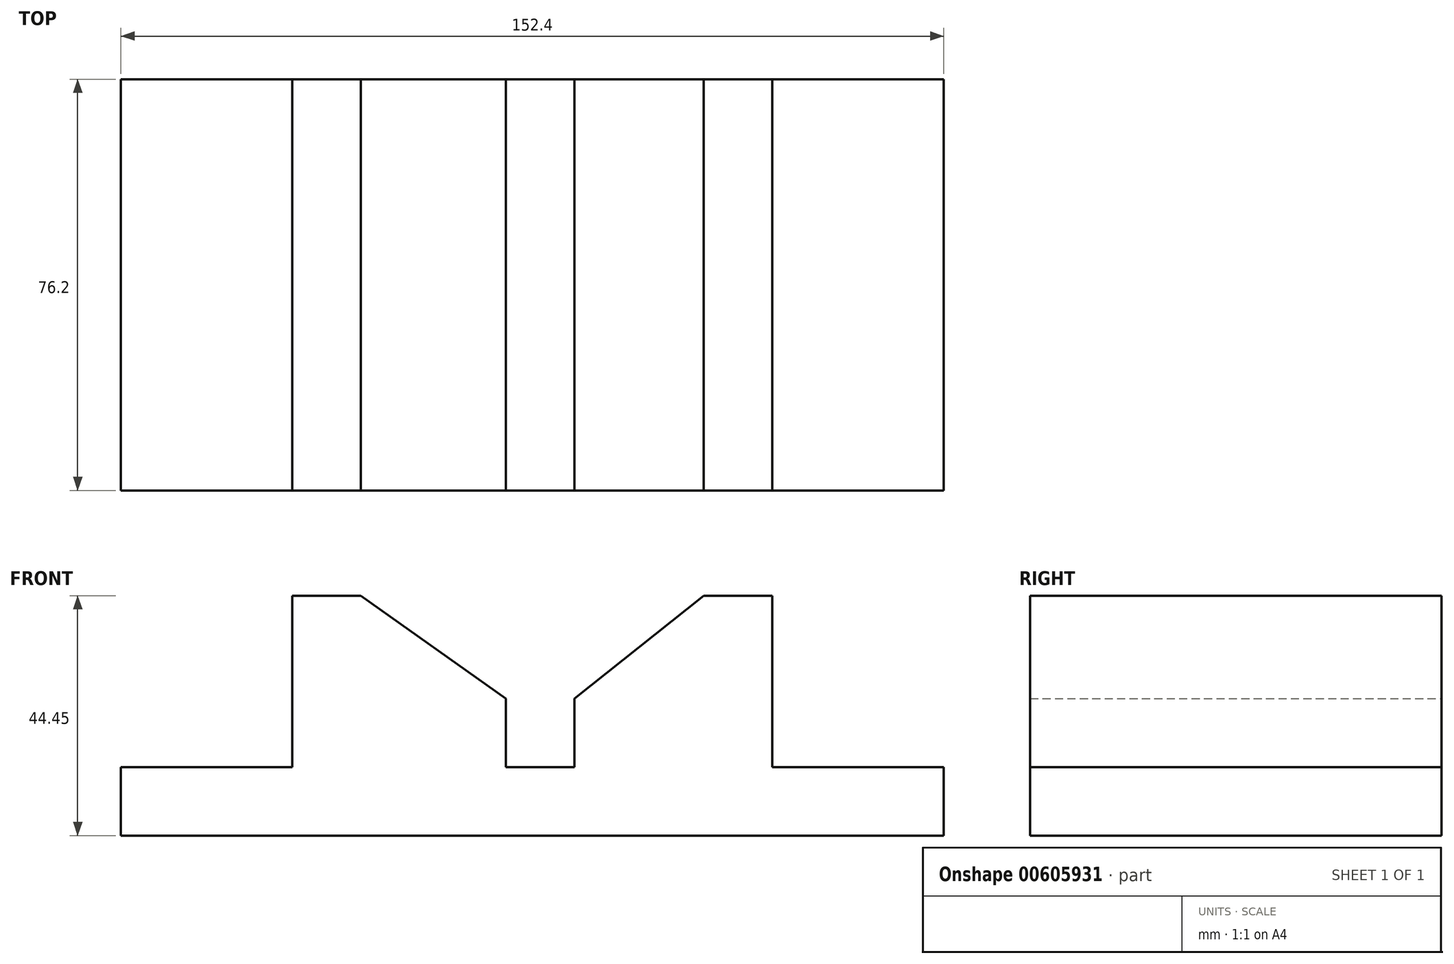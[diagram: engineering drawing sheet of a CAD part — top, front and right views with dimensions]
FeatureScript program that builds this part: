
annotation { "Feature Type Name" : "Feature", "Feature Type Description" : "" }
export const myFeature = defineFeature(function(context is Context, id is Id, definition is map)
    precondition{}
    {
        {
            var Q0;
            Q0=qCreatedBy(makeId("Front.planeOp"),FACE);
            var sketch = newSketch(context, id + "F0", { "sketchPlane" : qUnion([Q0])});
            skLineSegment(sketch, "E0", {"start": v(-199.14, -44.45) * mm, "end": v(-46.74, -44.45) * mm});
            skLineSegment(sketch, "E1", {"start": v(-46.74, -44.45) * mm, "end": v(-46.74, -31.75) * mm});
            skLineSegment(sketch, "E2", {"start": v(-46.74, -31.75) * mm, "end": v(-78.5, -31.75) * mm});
            skLineSegment(sketch, "E3", {"start": v(-78.5, -31.75) * mm, "end": v(-78.5, 0) * mm});
            skLineSegment(sketch, "E4", {"start": v(-78.5, 0) * mm, "end": v(-91.2, 0) * mm});
            skLineSegment(sketch, "E5", {"start": v(-199.14, -44.45) * mm, "end": v(-199.14, -31.75) * mm});
            skLineSegment(sketch, "E6", {"start": v(-199.14, -31.75) * mm, "end": v(-167.4, -31.75) * mm});
            skLineSegment(sketch, "E7", {"start": v(-167.4, -31.75) * mm, "end": v(-167.4, 0) * mm});
            skLineSegment(sketch, "E8", {"start": v(-167.4, 0) * mm, "end": v(-154.7, 0) * mm});
            skPoint(sketch, "E9.endSnap0", {"position": v(-183.27, -31.75) * mm});
            skLineSegment(sketch, "E10", {"start": v(-121.5, -31.75) * mm, "end": v(-115.15, -31.75) * mm});
            skLineSegment(sketch, "E11", {"start": v(-121.5, -31.75) * mm, "end": v(-127.85, -31.75) * mm});
            skLineSegment(sketch, "E12", {"start": v(-127.85, -31.75) * mm, "end": v(-127.85, -19.05) * mm});
            skLineSegment(sketch, "E13", {"start": v(-115.15, -31.75) * mm, "end": v(-115.15, -19.05) * mm});
            skLineSegment(sketch, "E14", {"start": v(-115.15, -19.05) * mm, "end": v(-91.2, 0) * mm});
            skLineSegment(sketch, "E15", {"start": v(-154.7, 0) * mm, "end": v(-127.85, -19.05) * mm});
            skSolve(sketch);
        }
        {
            var Q0;
            Q0=makeQuery(id+"F0.imprint","IMPRINT",FACE,{"disambiguationData":[TD([[makeQuery(id+"F0.imprint","IMPRINT",EDGE,{"derivedFrom":sQuery(id+"F0.wireOp",EDGE,"E0")}),1.0]])]});
            extrude(context, id + "F1", {"entities" : qUnion([Q0]), "depth" : 76.2 * mm, "offsetDistance" : 25.4 * mm});
        }
    });
